# Revit family: IS_Contour21_S6884_BIM_ES
name_source: partatom
category: Plumbing Fixtures
revit_build: Autodesk Revit 2017 (Build: 20160225_1515(x64)
units: mm (PartAtom-declared; Revit-internal decimal feet)

## family parameters
Always vertical = No
Cut with Voids When Loaded = No
OmniClass Number = 23.45.00.00
OmniClass Title = Sanitary, Laundry, and Cleaning Equipment
Part Type = Normal
Room Calculation Point = No
Round Connector Dimension = Use Diameter
Shared = No
Work Plane-Based = No

## types (1)
- S688467 - BCKREST NO FIN PADDED
    Acabado = Neutro
    Accesorios = www.idealstandard.es
    AlturaNominal = 70 mm  [stored 0.229659 ft]
    AnchuraNominal = 230 mm  [stored 0.754593 ft]
    Autor = Ideal Standard s.l.u. (ESP)
    Ayuda = https://www.idealstandard.es
    Cost = 0 $
    CódigoDeBarras = 5012001218471
    DescripciónUniclass2015 = Washbasin taps
    Description = BCKREST NO FIN PADDED
    Destacado = C21 COJIN BLANCO
    Dimensiones = 160 x 0 x 483 mm
    DiámetroDeDesagüe = 0
    Espacio = Interno
    FechaDeCreación = 16/09/2020
    GarantíaDeLasPiezas = 5
    GarantíaPiezas = 5
    GrosorDelMaterial = 0
    GuíaDeInstallación = www.idealstandard.es
    IfcExportaComo = IfcSanitaryTerminalType
    InformaciónDeProducto = https://www.idealstandard.es
    Installation instructions = https://www.idealstandard.es
    LongitudNominal = 325 mm  [stored 1.06627 ft]
    Maneta = No
    Manufacturer = https://www.idealstandard.es
    Marca = Ideal Standard Iberia
    Model = S688467
    NivelDeDesbordamiento = 0
    Nombre = WCseatsandcovers_Contour21_S6884_IdealStandard
    NombreDeObjetoBim = IS_IdealStandard_WCseatsandcovers_Contour21_S6884
    NúmeroDeModelo = S688467
    PesoBruto = 0
    PesoNeto = 3.9
    PlatoDeDucha = No
    Product group = Shower fittings package
    ProfundidadNominal = 325 mm  [stored 1.06627 ft]
    Referencia = S6884
    ReferenciaDeModelo = C21 COJIN BLANCO
    ReferenciaUniclass2015 = Pr_40_20_87_98
    Repuestos = https://www.idealstandard.es
    Revisión = 1
    Teléfono = +34 93 561 80 00
    TestDePresión = 10 bar
    TipoDeConexión = Fontaneria
    TipoDeExportaciónIfc = IfcSanitaryTerminalType
    TipoDeGarantía = Garantía del Fabricante
    TipoDeGrifería = Monomando
    URL = https://www.idealstandard.es
    Uniclass 2015 Code = Pr_40_20_87_88
    Uniclass 2015 Name = Shower fittings package
    UnidadDeTiempo = año
    UnidadDeVolúmen = Litros
    UnidadDeÁrea = milímetros
    UnidadGarantía = año
    UnidadLineal = milímetros
    UnidadMonetaria = €
    UrlDelFabricante = https://www.idealstandard.es
    Versión = 1
    VersiónUniclass2015 = v1.1

note: [stored X ft] marks values corroborated as IEEE doubles in the binary element streams (Revit-internal decimal feet)

## geometry (parser evidence)
native form markers: Sweep x2
no freeform markers — native parametric forms only
